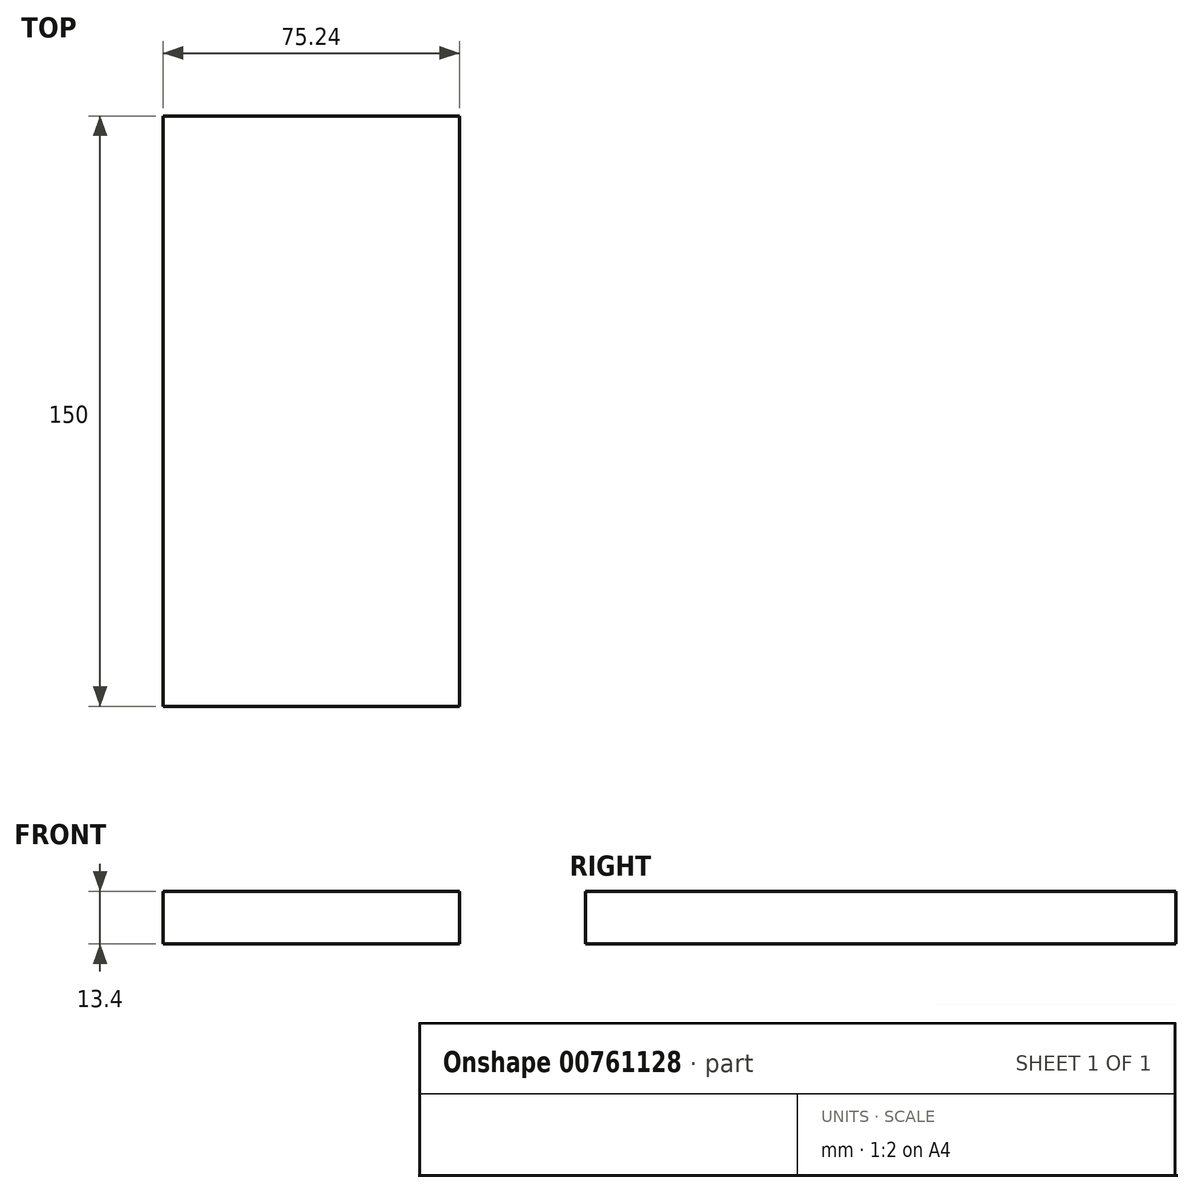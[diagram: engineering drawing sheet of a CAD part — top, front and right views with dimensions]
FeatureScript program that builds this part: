
annotation { "Feature Type Name" : "Feature", "Feature Type Description" : "" }
export const myFeature = defineFeature(function(context is Context, id is Id, definition is map)
    precondition{}
    {
        {
            assignVariable(context, id + "F0", {"name" : "p_height", "anyValue" : 150});
        }
        {
            var Q0;
            Q0=qCreatedBy(makeId("Front.planeOp"),FACE);
            var sketch = newSketch(context, id + "F1", { "sketchPlane" : qUnion([Q0])});
            skLineSegment(sketch, "E0.bottom", {"start": v(37.62, -6.7) * mm, "end": v(-37.62, -6.7) * mm});
            skLineSegment(sketch, "E0.top", {"start": v(37.62, 6.7) * mm, "end": v(-37.62, 6.7) * mm});
            skLineSegment(sketch, "E0.left", {"start": v(37.62, -6.7) * mm, "end": v(37.62, 6.7) * mm});
            skLineSegment(sketch, "E0.right", {"start": v(-37.62, -6.7) * mm, "end": v(-37.62, 6.7) * mm});
            skPoint(sketch, "E0.middle", {"position": v(0, 0) * mm});
            skSolve(sketch);
        }
        {
            var Q0;
            Q0=makeQuery(id+"F1.imprint","IMPRINT",FACE,{"disambiguationData":[TD([[makeQuery(id+"F1.imprint","IMPRINT",EDGE,{"derivedFrom":sQuery(id+"F1.wireOp",EDGE,"E0.bottom")}),-1.0]])]});
            extrude(context, id + "F2", {"entities" : qUnion([Q0]), "oppositeDirection" : true, "depth" : (getVariable(context, 'p_height')) * mm, "offsetDistance" : 25 * mm});
        }
    });
